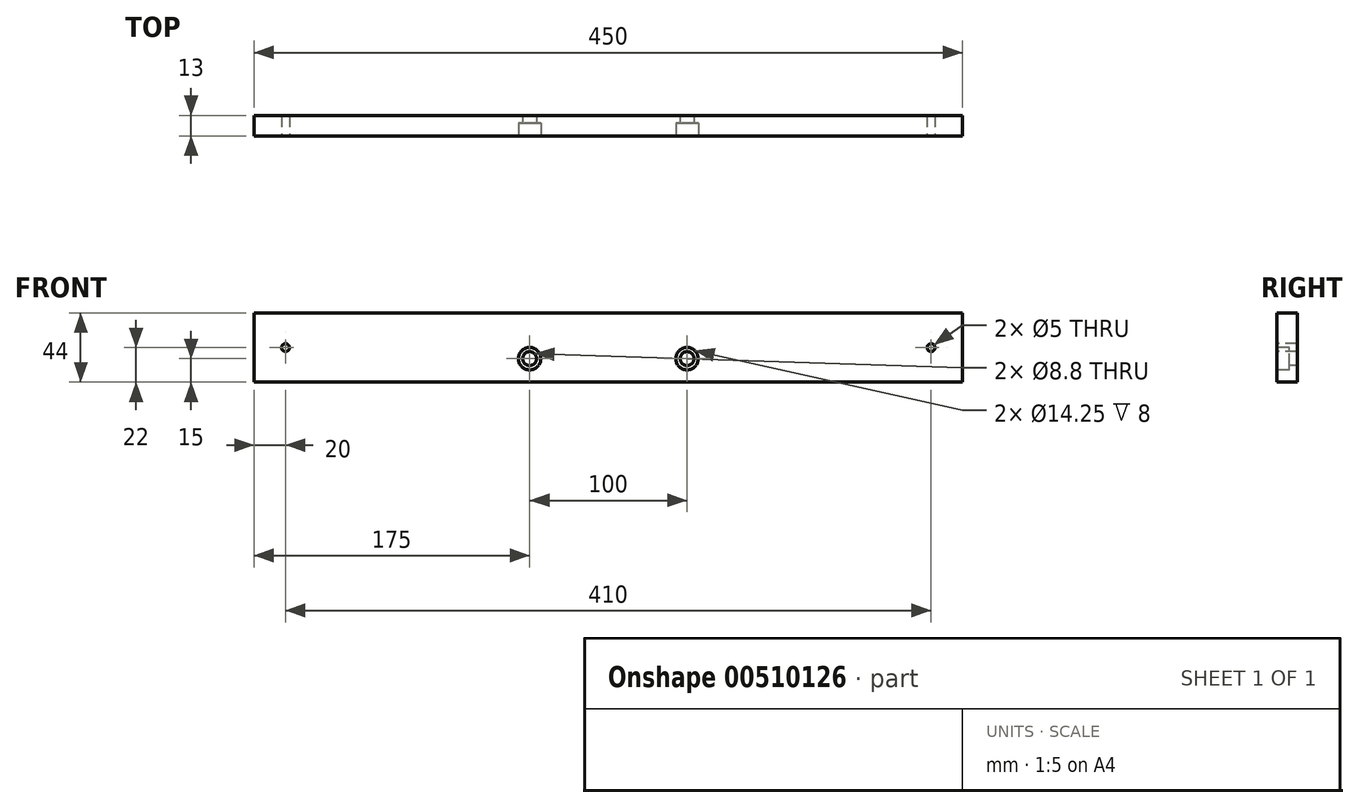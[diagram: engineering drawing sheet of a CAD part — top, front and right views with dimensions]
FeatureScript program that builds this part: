
annotation { "Feature Type Name" : "Feature", "Feature Type Description" : "" }
export const myFeature = defineFeature(function(context is Context, id is Id, definition is map)
    precondition{}
    {
        {
            var Q0;
            Q0=qCreatedBy(makeId("Front.planeOp"),FACE);
            var sketch = newSketch(context, id + "F0", { "sketchPlane" : qUnion([Q0])});
            skLineSegment(sketch, "E0.bottom", {"start": v(0, 0) * mm, "end": v(-450, 0) * mm});
            skLineSegment(sketch, "E0.top", {"start": v(0, 44) * mm, "end": v(-450, 44) * mm});
            skLineSegment(sketch, "E0.left", {"start": v(0, 0) * mm, "end": v(0, 44) * mm});
            skLineSegment(sketch, "E0.right", {"start": v(-450, 0) * mm, "end": v(-450, 44) * mm});
            skSolve(sketch);
        }
        {
            var Q0;
            Q0 = qSketchRegion(id + "F0", true);
            var Q1;
            Q1=makeQuery(id+"F0.imprint","IMPRINT",FACE,{"disambiguationData":[TD([[makeQuery(id+"F0.imprint","IMPRINT",EDGE,{"derivedFrom":sQuery(id+"F0.wireOp",EDGE,"E0.bottom")}),-1.0]])]});
            extrude(context, id + "F1", {"entities" : qUnion([Q0, Q1]), "depth" : 13 * mm});
        }
        {
            var Q0;
            Q0=makeQuery(id+"F1.opExtrude","CAP_FACE",FACE,{"disambiguationData":[OSD([sQuery(id+"F0.wireOp",EDGE,"E0.bottom"),sQuery(id+"F0.wireOp",EDGE,"E0.top"),sQuery(id+"F0.wireOp",EDGE,"E0.left"),sQuery(id+"F0.wireOp",EDGE,"E0.right")])],"isStart":false});
            var sketch = newSketch(context, id + "F2", { "sketchPlane" : qUnion([Q0])});
            skPoint(sketch, "E1", {"position": v(-20, 22) * mm});
            skPoint(sketch, "E2", {"position": v(-430, 22) * mm});
            skPoint(sketch, "E3", {"position": v(-275, 15) * mm});
            skPoint(sketch, "E4", {"position": v(-175, 15) * mm});
            skSolve(sketch);
        }
        {
            var Q0;
            Q0=sQuery(id+"F2.wireOp",VERTEX,"E2");
            var Q1;
            Q1=sQuery(id+"F2.wireOp",VERTEX,"E1");
            var Q2;
            Q2=makeQuery(id+"F1.opExtrude","SWEPT_BODY",BODY,{"disambiguationData":[OSD([sQuery(id+"F0.wireOp",EDGE,"E0.bottom"),sQuery(id+"F0.wireOp",EDGE,"E0.top"),sQuery(id+"F0.wireOp",EDGE,"E0.left"),sQuery(id+"F0.wireOp",EDGE,"E0.right")])]});
            hole(context, id + "F3", {"style" : HoleStyle.SIMPLE, "endStyle" : HoleEndStyle.THROUGH, "standardTappedOrClearance" : lookupTablePath({ "standard" : "ISO", "engagement" : "75%", "pitch" : "1 mm", "size" : "M6", "type" : "Tapped" }), "standardBlindInLast" : lookupTablePath({ "standard" : "ISO", "engagement" : "75%", "pitch" : "1 mm", "size" : "M6", "type" : "Tapped" }), "holeDiameter" : 5 * mm, "showTappedDepth" : true, "isTappedThrough" : true, "tappedDepth" : 50 * mm, "tapClearance" : 3, "startFromSketch" : true, "locations" : qUnion([Q0, Q1]), "scope" : qUnion([Q2]), "majorDiameter" : 6 * mm});
        }
        {
            var Q0;
            Q0=sQuery(id+"F2.wireOp",VERTEX,"E3");
            var Q1;
            Q1=sQuery(id+"F2.wireOp",VERTEX,"E4");
            var Q2;
            Q2=makeQuery(id+"F1.opExtrude","SWEPT_BODY",BODY,{"disambiguationData":[OSD([sQuery(id+"F0.wireOp",EDGE,"E0.bottom"),sQuery(id+"F0.wireOp",EDGE,"E0.top"),sQuery(id+"F0.wireOp",EDGE,"E0.left"),sQuery(id+"F0.wireOp",EDGE,"E0.right")])]});
            hole(context, id + "F4", {"style" : HoleStyle.C_BORE, "endStyle" : HoleEndStyle.THROUGH, "standardTappedOrClearance" : lookupTablePath({ "standard" : "ISO", "fit" : "Normal", "size" : "M8", "type" : "Clearance" }), "standardBlindInLast" : lookupTablePath({ "fit" : "Standard", "standard" : "ISO", "size" : "M8", "type" : "Clearance" }), "holeDiameter" : 8.8 * mm, "cBoreDiameter" : 14.25 * mm, "cBoreDepth" : 8 * mm, "isTappedThrough" : true, "tappedDepth" : 50 * mm, "tapClearance" : 3, "startFromSketch" : true, "locations" : qUnion([Q0, Q1]), "scope" : qUnion([Q2])});
        }
    });
